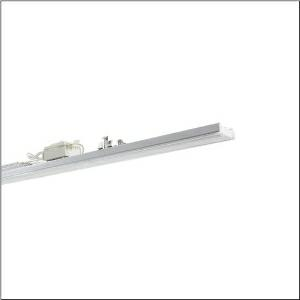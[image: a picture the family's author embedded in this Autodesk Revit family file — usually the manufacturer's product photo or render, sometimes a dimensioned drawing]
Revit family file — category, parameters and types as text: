
# Revit family: licross_21_recessed_ho_52tl1emn4e5s
name_source: partatom
category: Lighting Fixtures
units: mm (PartAtom-declared; Revit-internal decimal feet)

## family parameters
Cut with Voids When Loaded = No
Host = Face
Light Source = No
Part Type = Normal
Room Calculation Point = No
Round Connector Dimension = Use Diameter
Shared = No

## types (1)
- --- (1 x LED, 14710 lm, 83.1 W, 4000K)
    Apparent Load = 83 VA
    CIE Flux Codes = 85 95 99 100 100
    Color Rendering = 80
    Color Temperature = 4000K
    Default Elevation = 1800 mm
    Description = Licross 21 Recessed HO, luminaire insert, of sheet steel, galvanised, coil coated, white, length: 1.500mm, width: 66mm, height: 67mm, LED rated luminous flux: 14.710lm, light colour: 840, SDCM (Standard Deviation of Colour Matching)MacAdam ≤ 3 SDCM (initial), control gear: ON/OFF Multilumen, with plug, 3-pole, with phase selection, mains connection: 220..240V, AC, 50/60Hz, rated input power: 83W, internal wiring halogen-free, primary light control with lens, of plastic, primary optical cover: cover, of PMMA, light emission: direct distribution, primary light characteristic: symmetric, protection rating (complete): IP40, insulation class (complete): insulation class I (protective earthing), certification: CE, ENEC, VDE, UKCA, protection symbol: D if used in an environment without relevant dust loads with corresponding accessories, impact resistance: IK06, permissible ambient temperature for indoor applications: -35..+30°C, corresponds to IFS (International Featured Standards) requirements for safety and quality in the food industry, reducing of maximum allowable ambient temperature of 5°C with ceiling mounting, LABS conformity tested according to VDMA 24364:2018-05, The light source and the operating device comply with the requirements of the Ecodesign Regulation (EU) 2019/2020 and are replaceable in accordance with this regulation, packaging unit: 1 piece
    Height = 58 mm
    Lamp = 1 x LED
    Lamp Light Flux = 14710 lm
    Lamp Power = 83.1 W
    Lamp count = 1
    Length = 1500 mm
    Luminous efficacy = 177 lm/W
    Manufacturer = Siteco
    ModVariant = No
    Model = 52TL1EMN4E5S
    Mounting Place = Ceiling
    Mounting Type = Pendant
    Number of Poles = 1
    OnlyDefault = Yes
    Power Factor = 1
    Product Name = Licross 21 Recessed HO
    Product group = luminaire insert | ceiling pendant
    ProductGroupID = 901
    Protection Class = Protection class I
    Protection Degree = IP 40
    RLX_Detail_Level = 1
    RLX_Emergency_Light_Flux = 0 lm
    RLX_Emergency_Type = 0
    RLX_Emergency_Type_DB = No
    RlxData = <blob elided: 22649 chars, md5=4e93940f>
    Socket = socket
    Standby Power = 0 W
    System Light Flux = 14710 lm
    System Power = 83 W
    Type Comments = factory setting: luminous flux: 100 % | (A | C | E) | 195 mA
    Type Image = l_1296930.jpg
    URL = http://relux.com
    VarID = @adj_106439
    Voltage = 0 V
    Weight = 0.00 kg
    Width = 66 mm

## geometry (parser evidence)
native form markers: Blend x4, Sweep x11
no freeform markers — native parametric forms only
